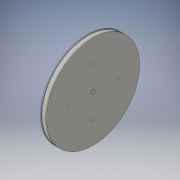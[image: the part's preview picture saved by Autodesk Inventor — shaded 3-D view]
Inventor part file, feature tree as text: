
AUTODESK INVENTOR PART (.ipt)
format: ipt  version: 2016 (Build 200138000, 138)  size: 123,904 bytes
history: native  units: in
note: dims shown in document units (in); Inventor stores cm internally (conversion verified against a paired STEP export)
features: sketch x5, extrude x3, hole x2
ambient origin geometry x8: Origin, YZ Plane, XZ Plane, XY Plane, X Axis, Y Axis, Z Axis, Center Point
bodies: Solid1 (feature_tree)
feature tree (10):
  extrude  "Extrusion1"  Depth=0.12in TaperAngle=0.0deg
  extrude  "Extrusion2"  Depth=0.02in TaperAngle=0.0deg
  extrude  "Extrusion3"  Depth=0.0394in
  hole  "Hole1"  [1 undecoded]
  hole  "Hole2"  [1 undecoded]
  sketch  "Sketch1"  dims[d0=2.4in d1=0.12in d2=0.0in]
  sketch  "Sketch2"  dims[d3=0.02in d4=0.0in d5=0.02in d6=0.0in]
  sketch  "Sketch3"  dims[d7=0.1024in]
  sketch  "Sketch4"  dims[d8=0.1024in d9=0.75in d10=0.375in d11=0.25in d12=0.5635in d13=1.0in d14=0.8108in d19=0.0394in]
  sketch  "Sketch5"  dims[d20=0.0394in d21=0.0394in d22=0.0394in d23=0.0394in d24=0.75in d25=0.375in d26=0.25in d27=0.5635in d28=1.0in d29=0.8108in]
note: 2 required parameter values undecoded (feature->parameter linkage not recoverable at this tier; creation-order binding heuristic only, values carry confidence <= 0.55)
